# Revit family: Haworth_Pergola_Slat_Laminate_Straight
name_source: partatom
category: Furniture Systems
revit_build: Autodesk Revit 2018 (Build: 20170223_1515(x64)
units: mm (PartAtom-declared; Revit-internal decimal feet)

## family parameters
Always vertical = Yes
Cut with Voids When Loaded = No
OmniClass Number = 23.40.70.14.64.21
OmniClass Title = Systems Furniture
Part Type = Normal
Room Calculation Point = No
Round Connector Dimension = Use Diameter
Shared = No
Work Plane-Based = No

## types (5) — shared parameters
Actual Depth = 4"
Actual Height = 89 1/2"
Assembly Code = E2020200
Base Height = 2"
Bracket Thickness = 25/128"
Custom Size = No
Description = Haworth - Pergola Slat - Laminate Straight
End Slat Offset = 3"
Manufacturer = Haworth
Max. Height = 89 1/2"
Max. Width = 144"
Min. Height = 89 1/2"
Min. Width = 48"
Model = Haworth Pergola
Revision Number = 1
Size = Verify Final Dim. w/ Haworth
Slat Finish = Haworth _ Paint _ Undecided _ Pergola
Standard Width = 48, 72, 96, 120, 144 in.
Sustainability Info = http://www.haworth.com
Trim Finish = Haworth _ Paint _ Undecided _ Pergola
URL = http://www.haworth.com
URL - Product = https://www.haworth.com
Warranty = http://www.haworth.com

## per-type parameters (varying)
| type | Actual Width | Slat Count | Width |
| 144w | 144" | 24 | 144" |
| 120w | 120" | 20 | 120" |
| 72w | 72" | 12 | 72" |
| 96w | 96" | 16 | 96" |
| 48w | 48" | 8 | 48" |

## geometry (parser evidence)
native form markers: Sweep x7
no freeform markers — native parametric forms only
